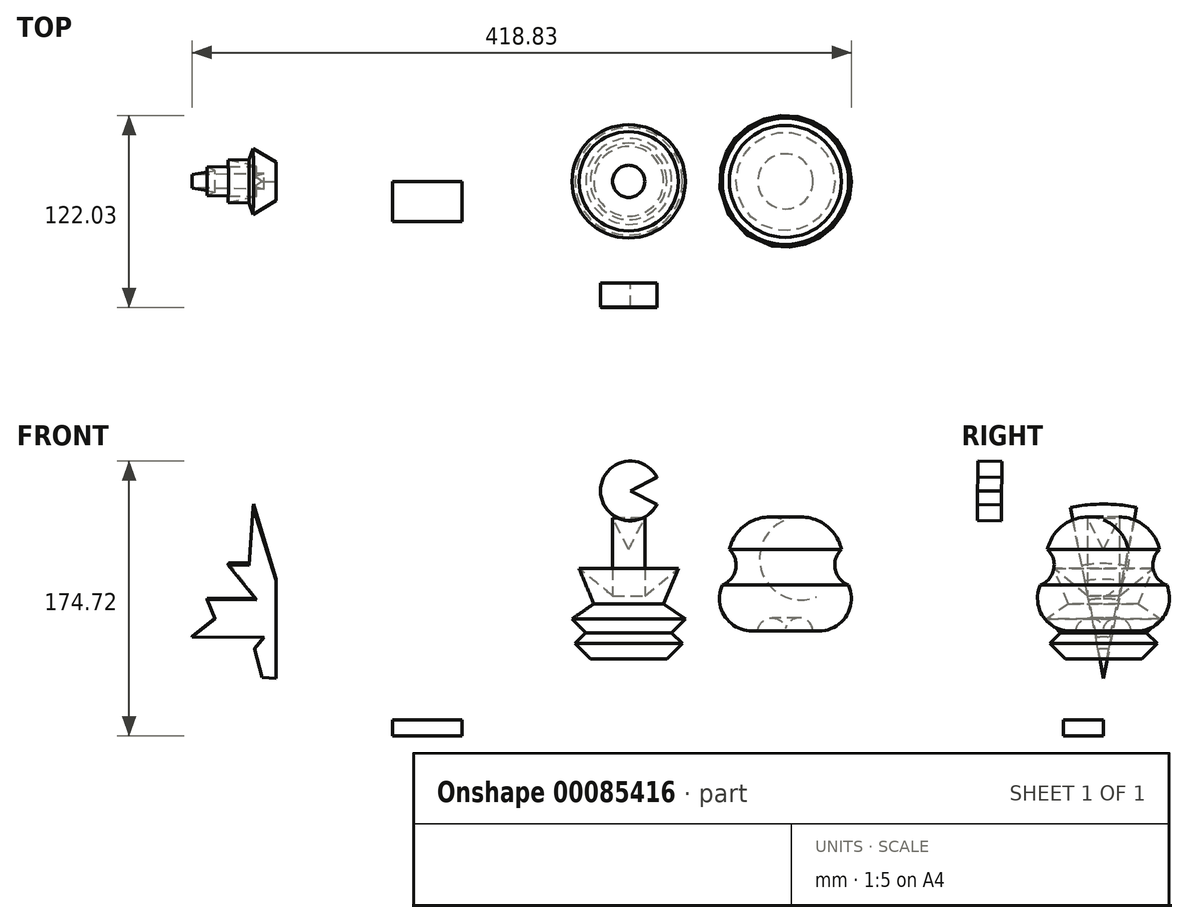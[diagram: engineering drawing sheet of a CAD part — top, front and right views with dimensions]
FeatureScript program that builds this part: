
annotation { "Feature Type Name" : "Feature", "Feature Type Description" : "" }
export const myFeature = defineFeature(function(context is Context, id is Id, definition is map)
    precondition{}
    {
        {
            var Q0;
            Q0=qCreatedBy(makeId("Front.planeOp"),FACE);
            var sketch = newSketch(context, id + "F0", { "sketchPlane" : qUnion([Q0])});
            skLineSegment(sketch, "E0", {"start": v(-60.43, -76.26) * mm, "end": v(-70.23, -66.46) * mm});
            skLineSegment(sketch, "E1", {"start": v(-70.23, -66.46) * mm, "end": v(-63.4, -59.64) * mm});
            skLineSegment(sketch, "E2", {"start": v(-63.4, -59.64) * mm, "end": v(-72.14, -50.9) * mm});
            skLineSegment(sketch, "E3", {"start": v(-72.14, -50.9) * mm, "end": v(-58.3, -41.32) * mm});
            skLineSegment(sketch, "E4", {"start": v(-58.3, -41.32) * mm, "end": v(-67.67, -18.73) * mm});
            skLineSegment(sketch, "E5", {"start": v(-67.67, -18.73) * mm, "end": v(-46.36, -36.2) * mm});
            skLineSegment(sketch, "E6", {"start": v(-46.36, -36.2) * mm, "end": v(-46.36, 13.23) * mm});
            skLineSegment(sketch, "E7", {"start": v(-46.36, 13.23) * mm, "end": v(-36.14, -6.8) * mm});
            skLineSegment(sketch, "E8", {"start": v(-36.14, -6.8) * mm, "end": v(-36.14, 36.66) * mm});
            skLineSegment(sketch, "E9", {"start": v(-60.43, -76.26) * mm, "end": v(-36.14, -76.26) * mm});
            skLineSegment(sketch, "E10", {"start": v(-36.14, -76.26) * mm, "end": v(-36.14, 36.66) * mm});
            skSolve(sketch);
        }
        {
            var Q0;
            Q0=makeQuery(id+"F0.imprint","IMPRINT",FACE,{"disambiguationData":[TD([[makeQuery(id+"F0.imprint","IMPRINT",EDGE,{"derivedFrom":sQuery(id+"F0.wireOp",EDGE,"E0")}),-1.0]])]});
            var Q1;
            Q1=sQuery(id+"F0.wireOp",EDGE,"E10");
            revolve(context, id + "F1", {"entities" : qUnion([Q0]), "axis" : qUnion([Q1]), "revolveType" : RevolveType.FULL});
        }
        {
            var Q0;
            Q0=qCreatedBy(makeId("Front.planeOp"),FACE);
            var sketch = newSketch(context, id + "F2", { "sketchPlane" : qUnion([Q0])});
            skArc(sketch, "E11", {"start": v(45.93, -58.3) * mm, "mid": v(53.28, -67.88) * mm, "end": v(63.41, -61.32) * mm});
            skArc(sketch, "E12", {"start": v(23.32, -29.37) * mm, "mid": v(25.93, -50.64) * mm, "end": v(45.93, -58.3) * mm});
            skArc(sketch, "E13", {"start": v(23.32, -29.37) * mm, "mid": v(31.81, -19.31) * mm, "end": v(27.84, -6.76) * mm});
            skArc(sketch, "E14", {"start": v(63.41, 11.93) * mm, "mid": v(41.3, 10.84) * mm, "end": v(27.84, -6.76) * mm});
            skLineSegment(sketch, "E15", {"start": v(63.41, 11.93) * mm, "end": v(63.41, -61.32) * mm});
            skSolve(sketch);
        }
        {
            var Q0;
            Q0=makeQuery(id+"F2.imprint","IMPRINT",FACE,{"disambiguationData":[TD([[makeQuery(id+"F2.imprint","IMPRINT",EDGE,{"derivedFrom":sQuery(id+"F2.wireOp",EDGE,"E11")}),1.0]])]});
            var Q1;
            Q1=sQuery(id+"F2.wireOp",EDGE,"E15");
            revolve(context, id + "F3", {"entities" : qUnion([Q0]), "axis" : qUnion([Q1]), "revolveType" : RevolveType.FULL});
        }
        {
            var Q0;
            Q0=qCreatedBy(makeId("Front.planeOp"),FACE);
            var sketch = newSketch(context, id + "F4", { "sketchPlane" : qUnion([Q0])});
            skLineSegment(sketch, "E16.bottom", {"start": v(-182.4, -60.1) * mm, "end": v(-163.48, -60.1) * mm});
            skLineSegment(sketch, "E16.top", {"start": v(-182.4, -75.33) * mm, "end": v(-163.48, -75.33) * mm});
            skLineSegment(sketch, "E16.left", {"start": v(-182.4, -60.1) * mm, "end": v(-182.4, -75.33) * mm});
            skLineSegment(sketch, "E16.right", {"start": v(-163.48, -60.1) * mm, "end": v(-163.48, -75.33) * mm});
            skSolve(sketch);
        }
        {
            var Q0;
            Q0=makeQuery(id+"F4.imprint","IMPRINT",FACE,{"disambiguationData":[TD([[makeQuery(id+"F4.imprint","IMPRINT",EDGE,{"derivedFrom":sQuery(id+"F4.wireOp",EDGE,"E16.bottom")}),-1.0]])]});
            var Q1;
            Q1=sQuery(id+"F4.wireOp",EDGE,"E16.right");
            revolve(context, id + "F5", {"entities" : qUnion([Q0]), "axis" : qUnion([Q1]), "revolveType" : RevolveType.SYMMETRIC, "angle" : 305.32 * degree});
        }
        {
            var Q0;
            Q0=qCreatedBy(makeId("Front.planeOp"),FACE);
            var sketch = newSketch(context, id + "F6", { "sketchPlane" : qUnion([Q0])});
            skLineSegment(sketch, "E17.bottom", {"start": v(-186.05, -114.9) * mm, "end": v(-141.9, -114.9) * mm});
            skLineSegment(sketch, "E17.top", {"start": v(-186.05, -125.32) * mm, "end": v(-141.9, -125.32) * mm});
            skLineSegment(sketch, "E17.left", {"start": v(-186.05, -114.9) * mm, "end": v(-186.05, -125.32) * mm});
            skLineSegment(sketch, "E17.right", {"start": v(-141.9, -114.9) * mm, "end": v(-141.9, -125.32) * mm});
            skSolve(sketch);
        }
        {
            var Q0;
            Q0=makeQuery(id+"F6.imprint","IMPRINT",FACE,{"disambiguationData":[TD([[makeQuery(id+"F6.imprint","IMPRINT",EDGE,{"derivedFrom":sQuery(id+"F6.wireOp",EDGE,"E17.bottom")}),-1.0]])]});
            extrude(context, id + "F7", {"entities" : qUnion([Q0]), "depth" : 25.4 * mm});
        }
        {
            var Q0;
            Q0=makeQuery(id+"F5.opRevolve","SWEPT_BODY",BODY,{"disambiguationData":[OSD([sQuery(id+"F4.wireOp",EDGE,"E16.bottom"),sQuery(id+"F4.wireOp",EDGE,"E16.top"),sQuery(id+"F4.wireOp",EDGE,"E16.left"),sQuery(id+"F4.wireOp",EDGE,"E16.right")])]});
            var Q1;
            Q1=makeQuery(id+"F7.opExtrude","CAP_EDGE",EDGE,{"disambiguationData":[OSD([sQuery(id+"F6.wireOp",EDGE,"E17.bottom")])],"isStart":false});
            transform(context, id + "F8", {"entities" : qUnion([Q0]), "transformType" : TransformType.ROTATION, "transformAxis" : qUnion([Q1]), "angle" : 89.4 * degree, "makeCopy" : false});
        }
        {
            var Q0;
            Q0=makeQuery(id+"F5.opRevolve","SWEPT_BODY",BODY,{"disambiguationData":[OSD([sQuery(id+"F4.wireOp",EDGE,"E16.bottom"),sQuery(id+"F4.wireOp",EDGE,"E16.top"),sQuery(id+"F4.wireOp",EDGE,"E16.left"),sQuery(id+"F4.wireOp",EDGE,"E16.right")])]});
            transform(context, id + "F9", {"entities" : qUnion([Q0]), "transformType" : TransformType.TRANSLATION_3D, "dx" : 128.36 * mm, "dy" : 0 * mm, "dz" : 119.4 * mm, "makeCopy" : false});
        }
        {
            var Q0;
            Q0=qCreatedBy(makeId("Front.planeOp"),FACE);
            var sketch = newSketch(context, id + "F10", { "sketchPlane" : qUnion([Q0])});
            skLineSegment(sketch, "E18", {"start": v(-268.86, -87.96) * mm, "end": v(-273.64, -69.63) * mm});
            skLineSegment(sketch, "E19", {"start": v(-273.64, -69.63) * mm, "end": v(-267.66, -62.06) * mm});
            skLineSegment(sketch, "E20", {"start": v(-267.66, -62.06) * mm, "end": v(-313.48, -62.06) * mm});
            skLineSegment(sketch, "E21", {"start": v(-313.48, -62.06) * mm, "end": v(-298.74, -50.11) * mm});
            skLineSegment(sketch, "E22", {"start": v(-298.74, -50.11) * mm, "end": v(-303.92, -37.76) * mm});
            skLineSegment(sketch, "E23", {"start": v(-303.92, -37.76) * mm, "end": v(-272.44, -37.76) * mm});
            skLineSegment(sketch, "E24", {"start": v(-272.44, -37.76) * mm, "end": v(-290.37, -15.45) * mm});
            skLineSegment(sketch, "E25", {"start": v(-290.37, -15.45) * mm, "end": v(-277.22, -15.45) * mm});
            skLineSegment(sketch, "E26", {"start": v(-277.22, -15.45) * mm, "end": v(-274.43, 22) * mm});
            skLineSegment(sketch, "E27", {"start": v(-274.43, 22) * mm, "end": v(-260.09, -25.4) * mm});
            skLineSegment(sketch, "E28", {"start": v(-260.09, -25.4) * mm, "end": v(-260.09, -88.76) * mm});
            skLineSegment(sketch, "E29", {"start": v(-268.86, -87.96) * mm, "end": v(-260.09, -88.76) * mm});
            skSolve(sketch);
        }
        {
            var Q0;
            Q0=makeQuery(id+"F10.imprint","IMPRINT",FACE,{"disambiguationData":[TD([[makeQuery(id+"F10.imprint","IMPRINT",EDGE,{"derivedFrom":sQuery(id+"F10.wireOp",EDGE,"E18")}),-1.0]])]});
            var Q1;
            Q1=sQuery(id+"F10.wireOp",EDGE,"E29");
            revolve(context, id + "F11", {"entities" : qUnion([Q0]), "axis" : qUnion([Q1]), "revolveType" : RevolveType.SYMMETRIC, "angle" : 22.2 * degree});
        }
    });
